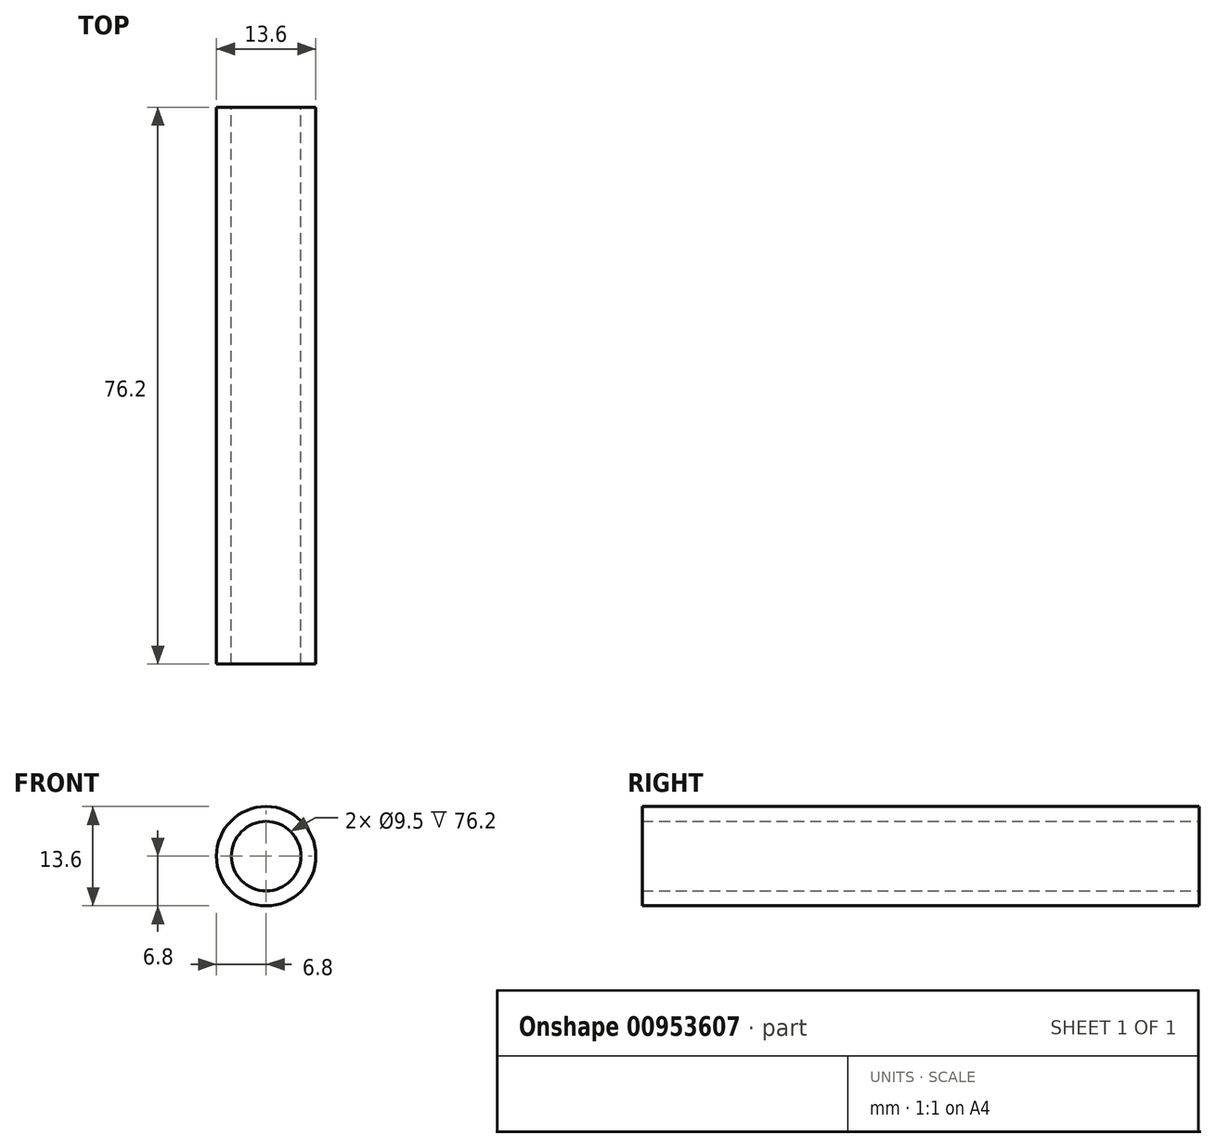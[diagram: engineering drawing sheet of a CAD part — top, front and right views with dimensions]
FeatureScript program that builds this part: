
annotation { "Feature Type Name" : "Feature", "Feature Type Description" : "" }
export const myFeature = defineFeature(function(context is Context, id is Id, definition is map)
    precondition{}
    {
        {
            var Q0;
            Q0=qCreatedBy(makeId("Front.planeOp"),FACE);
            var sketch = newSketch(context, id + "F0", { "sketchPlane" : qUnion([Q0])});
            skCircle(sketch, "E0", {"center": v(0, 0) * mm, "radius": 6.8 * mm});
            skCircle(sketch, "E1", {"center": v(0, 0) * mm, "radius": 4.75 * mm});
            skSolve(sketch);
        }
        {
            var Q0;
            Q0=makeQuery(id+"F0.imprint","IMPRINT",FACE,{"disambiguationData":[TD([[makeQuery(id+"F0.imprint","IMPRINT",EDGE,{"derivedFrom":sQuery(id+"F0.wireOp",EDGE,"E0")}),1.0]])]});
            extrude(context, id + "F1", {"entities" : qUnion([Q0]), "depth" : 76.2 * mm, "offsetDistance" : 25.4 * mm});
        }
    });
